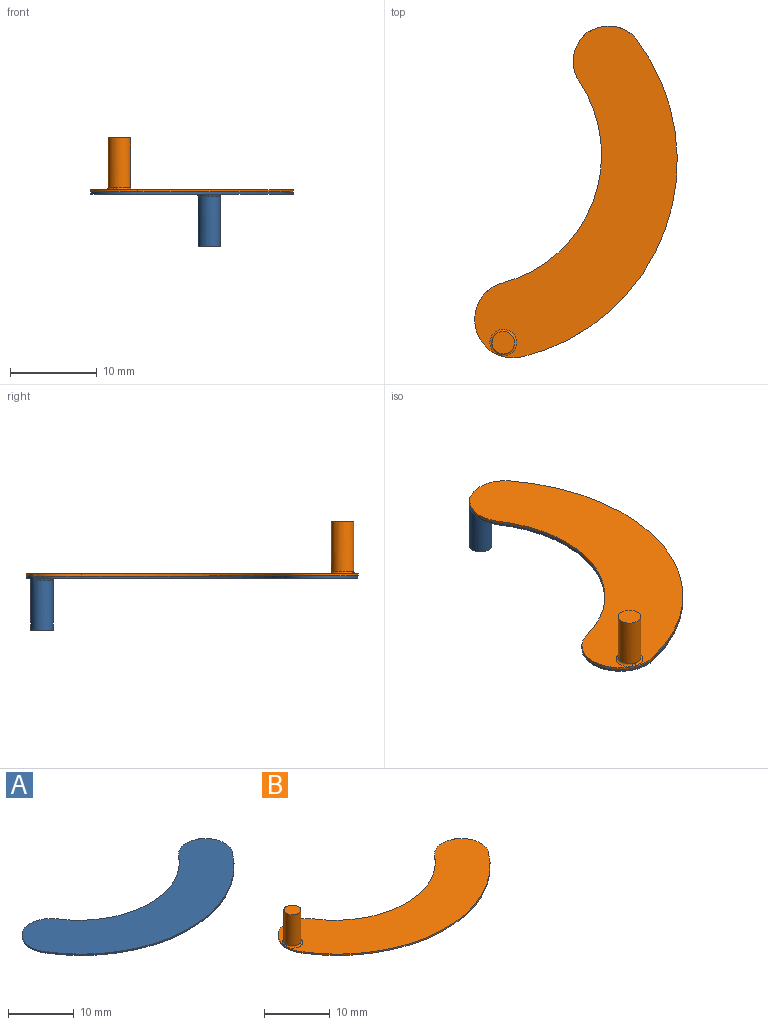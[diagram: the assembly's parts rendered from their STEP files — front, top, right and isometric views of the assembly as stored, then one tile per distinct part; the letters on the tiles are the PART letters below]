
ASSEMBLY  parts=2 mates=1
PART A: 10 faces, bbox 40.3x18x6.3 mm
  f0: cylinder r=4.1mm len=5.46mm, axis (0,0,-1), area 1.5mm2, adj f4,f5,f6,f7,f9
  f1: cylinder r=4.1mm len=5.08mm, axis (0,0,-1), area 1.4mm2, adj f3,f5,f6,f7,f9
  f2: cylinder r=4.42mm len=8.16mm, axis (0,0,-1), area 3.4mm2, adj f3,f4,f5,f6
  f3: cylinder r=15.27mm len=24.83mm, axis (0,0,-1), area 7.3mm2, adj f1,f2,f5,f6
  f4: cylinder r=23.27mm len=38.91mm, axis (0,0,-1), area 11.5mm2, adj f0,f2,f5,f6
  f5: plane 40.3x18.04mm, normal (0,0,1), area 386.4mm2, adj f0,f1,f2,f3,f4,f7
  f6: plane 40.3x18.04mm, normal (0,0,-1), area 379.3mm2, adj f0,f1,f2,f3,f4,f9
  f7: cylinder r=1.3mm len=6.25mm, axis (0,0,1), area 47.5mm2, adj f0,f1,f5,f8,f9
  f8: plane 2.6x2.6mm, normal (0,0,-1), area 5.3mm2, adj f7
  f9: torus R=1.55mm, axis (0,0,-1), area 2.8mm2, adj f0,f1,f6,f7
PART B: 12 faces, bbox 40.6x18x6.3 mm
  f0: cylinder r=4.1mm len=5.46mm, axis (0,0,-1), area 1.5mm2, adj f4,f5,f6,f7
  f1: cylinder r=4.1mm len=5.08mm, axis (0,0,-1), area 1.4mm2, adj f3,f5,f6,f7
  f2: cylinder r=4.42mm len=8.16mm, axis (0,0,-1), area 3.4mm2, adj f3,f4,f5,f6,f11
  f3: cylinder r=15.27mm len=24.83mm, axis (0,0,-1), area 7.3mm2, adj f1,f2,f5,f6
  f4: cylinder r=23.27mm len=38.91mm, axis (0,0,-1), area 11.5mm2, adj f0,f2,f5,f6
  f5: plane 40.3x18.04mm, normal (0,0,1), area 378.9mm2, adj f0,f1,f2,f3,f4,f7,f10
  f6: plane 40.3x18.04mm, normal (0,0,-1), area 386.4mm2, adj f0,f1,f2,f3,f4,f7
  f7: cylinder r=1.3mm len=0.85mm, axis (0,0,1), area 0.3mm2, adj f0,f1,f5,f6
  f8: cylinder r=1.3mm len=5.75mm, axis (0,0,-1), area 47mm2, adj f9,f10,f11
  f9: plane 2.6x2.6mm, normal (0,0,1), area 5.3mm2, adj f8
  f10: torus R=1.55mm, axis (0,0,-1), area 3.3mm2, adj f5,f8,f11
  f11: bspline ~0.57x0.3mm, area 0.1mm2, adj f2,f8,f10
PLACE A rot(axis=(0,0,1),72.4deg) t=(25.61,-7.49,11.8)mm
PLACE B rot(axis=(0,0,1),72.4deg) t=(-5.46,2.38,11.8)mm
MATE fastened A.f5 <-> B.f6  axis (0,0,1) through (9.42,-3.75,12.05)mm
